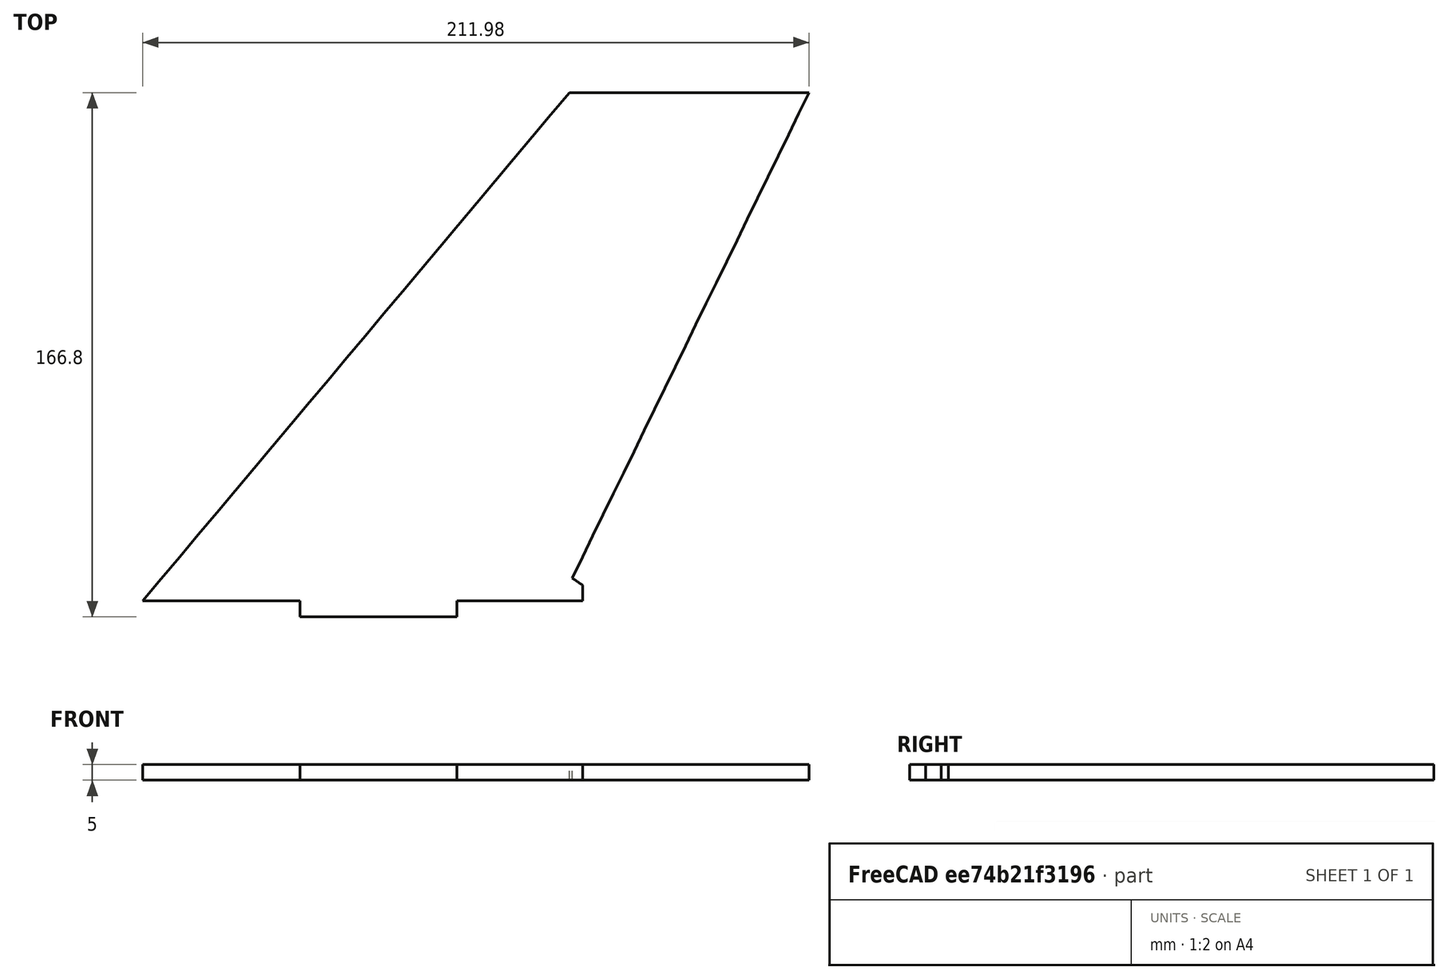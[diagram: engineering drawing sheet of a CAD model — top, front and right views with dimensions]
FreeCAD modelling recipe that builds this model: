
FCSTD DOCUMENT  (FreeCAD 0.19R)
Label: F-35_v2_parts_4
License: All rights reserved
LicenseURL: http://en.wikipedia.org/wiki/All_rights_reserved
objects: App::DocumentObjectGroup×2, PartDesign::CoordinateSystem×2, App::FeaturePython×1, Sketcher::SketchObject×1, PartDesign::Pad×1, PartDesign::Body×1, App::Part×1
note: 6 computed .brp shape members not serialized (recipe doc carries the construction recipe); baked Part::Feature solids carry a one-line shape summary decoded from their .brp

FEATURE [App::DocumentObjectGroup] Parts
FEATURE [PartDesign::CoordinateSystem] LCS_Origin
  AttacherType = Attacher::AttachEngine3D
  MapMode = 2
  Support = -> [X_Axis]
FEATURE [App::DocumentObjectGroup] Constraints
FEATURE [App::FeaturePython] Variables  # WARN: FeaturePython — macro-defined, semantics opaque (R4)
FEATURE [Sketcher::SketchObject] Sketch003
  FullyConstrained = false
  sketch-geometry (10):
    g0: BSplineCurve PolesCount=2 KnotsCount=2 Degree=1 IsPeriodic=0
    g1: BSplineCurve PolesCount=2 KnotsCount=2 Degree=1 IsPeriodic=0
    g2: BSplineCurve PolesCount=2 KnotsCount=2 Degree=1 IsPeriodic=0
    g3: BSplineCurve PolesCount=2 KnotsCount=2 Degree=1 IsPeriodic=0
    g4: BSplineCurve PolesCount=2 KnotsCount=2 Degree=1 IsPeriodic=0
    g5: BSplineCurve PolesCount=2 KnotsCount=2 Degree=1 IsPeriodic=0
    g6: BSplineCurve PolesCount=2 KnotsCount=2 Degree=1 IsPeriodic=0
    g7: BSplineCurve PolesCount=2 KnotsCount=2 Degree=1 IsPeriodic=0
    g8: BSplineCurve PolesCount=2 KnotsCount=2 Degree=1 IsPeriodic=0
    g9: BSplineCurve PolesCount=2 KnotsCount=2 Degree=1 IsPeriodic=0
FEATURE [PartDesign::Pad] Pad003
  Direction = (1,1,1)
  Length = 5
  Length2 = 100
  Profile = -> Sketch003
  Type = 0
FEATURE [PartDesign::Body] Body003  label="Part4"
  Group = -> [Sketch003,Pad003]
  Origin = -> Origin004
  Tip = -> Pad003
FEATURE [PartDesign::CoordinateSystem] LCS_1
  AttacherType = Attacher::AttachEngine3D
  AttachmentOffset = pos=(0,0,0) rot=(0,0,1;0.331613rad)
  MapMode = 45
  Placement = pos=(743.703,-616.072,2.5) rot=(0.702208,-0.117509,0.702208;3.37554rad)
  Support = -> [Pad003]
FEATURE [App::Part] Model
  Configuration = 0
  Group = -> [LCS_Origin,Constraints,Variables,Body003,LCS_1]
  Origin = -> Origin
  Type = Assembly4 Model
